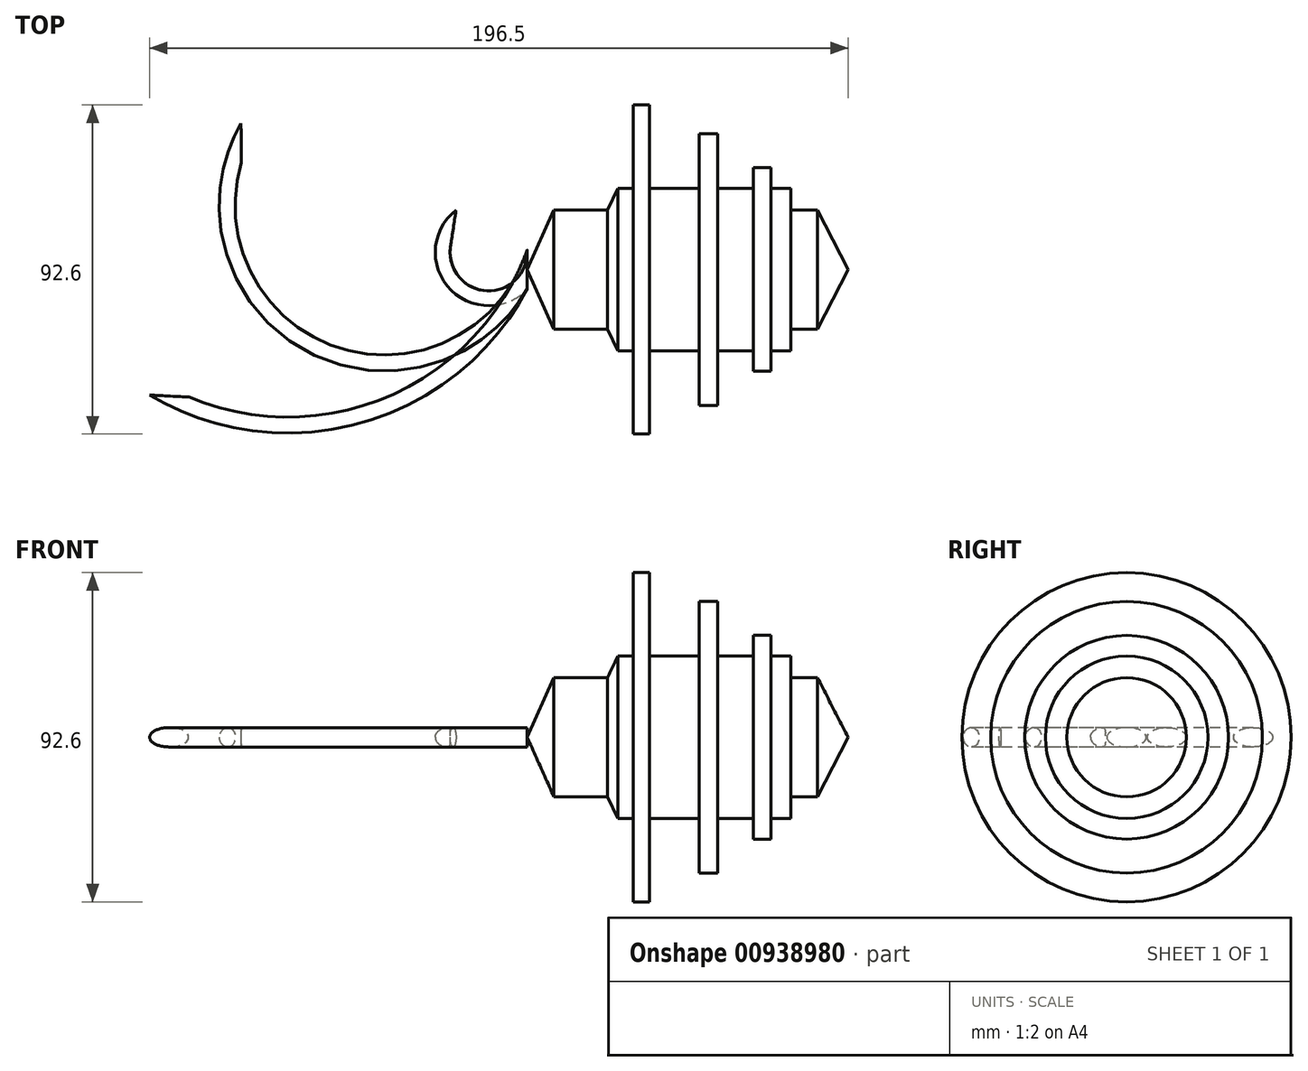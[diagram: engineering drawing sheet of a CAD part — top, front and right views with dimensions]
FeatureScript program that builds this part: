
annotation { "Feature Type Name" : "Feature", "Feature Type Description" : "" }
export const myFeature = defineFeature(function(context is Context, id is Id, definition is map)
    precondition{}
    {
        {
            var Q0;
            Q0=qCreatedBy(makeId("Top.planeOp"),FACE);
            var sketch = newSketch(context, id + "F0", { "sketchPlane" : qUnion([Q0])});
            skLineSegment(sketch, "E0", {"start": v(0, 0) * mm, "end": v(7.52, 16.78) * mm});
            skLineSegment(sketch, "E1", {"start": v(7.52, 16.78) * mm, "end": v(22.57, 16.78) * mm});
            skLineSegment(sketch, "E2", {"start": v(22.57, 16.78) * mm, "end": v(25.46, 22.86) * mm});
            skLineSegment(sketch, "E3", {"start": v(25.46, 22.86) * mm, "end": v(29.8, 22.86) * mm});
            skLineSegment(sketch, "E4", {"start": v(29.8, 22.86) * mm, "end": v(29.8, 46.3) * mm});
            skLineSegment(sketch, "E5", {"start": v(29.8, 46.3) * mm, "end": v(34.43, 46.3) * mm});
            skLineSegment(sketch, "E6", {"start": v(34.43, 46.3) * mm, "end": v(34.43, 22.86) * mm});
            skLineSegment(sketch, "E7", {"start": v(34.43, 22.86) * mm, "end": v(48.32, 22.86) * mm});
            skLineSegment(sketch, "E8", {"start": v(48.32, 22.86) * mm, "end": v(48.32, 38.2) * mm});
            skLineSegment(sketch, "E9", {"start": v(48.32, 38.2) * mm, "end": v(53.53, 38.2) * mm});
            skLineSegment(sketch, "E10", {"start": v(53.53, 38.2) * mm, "end": v(53.53, 22.86) * mm});
            skLineSegment(sketch, "E11", {"start": v(53.53, 22.86) * mm, "end": v(63.66, 22.86) * mm});
            skLineSegment(sketch, "E12", {"start": v(63.66, 22.86) * mm, "end": v(63.66, 28.65) * mm});
            skLineSegment(sketch, "E13", {"start": v(63.66, 28.65) * mm, "end": v(68.58, 28.65) * mm});
            skLineSegment(sketch, "E14", {"start": v(68.58, 28.65) * mm, "end": v(68.58, 22.86) * mm});
            skLineSegment(sketch, "E15", {"start": v(68.58, 22.86) * mm, "end": v(74.08, 22.86) * mm});
            skLineSegment(sketch, "E16", {"start": v(74.08, 22.86) * mm, "end": v(74.08, 16.78) * mm});
            skLineSegment(sketch, "E17", {"start": v(74.08, 16.78) * mm, "end": v(81.6, 16.78) * mm});
            skLineSegment(sketch, "E18", {"start": v(81.6, 16.78) * mm, "end": v(90.28, 0) * mm});
            skArc(sketch, "E19", {"start": v(0, 0) * mm, "mid": v(-44.19, -7.67) * mm, "end": v(-34.72, 36.17) * mm});
            skArc(sketch, "E20", {"start": v(0, 0) * mm, "mid": v(-57.93, -22.23) * mm, "end": v(-80.44, 35.6) * mm});
            skArc(sketch, "E21", {"start": v(0, 0) * mm, "mid": v(-42.72, -39.37) * mm, "end": v(-100.7, -35.6) * mm});
            skArc(sketch, "E22", {"start": v(0, 0) * mm, "mid": v(-16.5, -5.59) * mm, "end": v(-20.83, 11.29) * mm});
            skLineSegment(sketch, "E23", {"start": v(0, 0) * mm, "end": v(90.28, 0) * mm});
            skSolve(sketch);
        }
        {
            var Q0;
            Q0=qCreatedBy(makeId("Right.planeOp"),FACE);
            var sketch = newSketch(context, id + "F1", { "sketchPlane" : qUnion([Q0])});
            skEllipse(sketch, "E24", {"center": v(0, 0) * mm, "majorRadius": 5.53 * mm, "minorRadius": 2.73 * mm, "majorAxis": v(-1, 0)});
            skSolve(sketch);
        }
        {
            var Q0;
            Q0=makeQuery(id+"F0.imprint","IMPRINT",FACE,{"disambiguationData":[TD([[makeQuery(id+"F0.imprint","IMPRINT",EDGE,{"derivedFrom":sQuery(id+"F0.wireOp",EDGE,"E0")}),-1.0]])]});
            var Q1;
            Q1=sQuery(id+"F0.wireOp",EDGE,"E23");
            revolve(context, id + "F2", {"surfaceOperationType" : NewSurfaceOperationType.NEW, "entities" : qUnion([Q0]), "axis" : qUnion([Q1]), "revolveType" : RevolveType.FULL});
        }
        {
            var Q0;
            Q0=makeQuery(id+"F1.imprint","IMPRINT",FACE,{"disambiguationData":[TD([[makeQuery(id+"F1.imprint","IMPRINT",EDGE,{"derivedFrom":sQuery(id+"F1.wireOp",EDGE,"E24")}),1.0]])]});
            var Q1;
            Q1=sQuery(id+"F0.wireOp",EDGE,"E22");
            sweep(context, id + "F3", {"profiles" : qUnion([Q0]), "path" : qUnion([Q1])});
        }
        {
            var Q0;
            Q0=makeQuery(id+"F3.opSweep","CAP_FACE",FACE,{"disambiguationData":[OSD([sQuery(id+"F0.wireOp",VERTEX,"E22.start"),sQuery(id+"F1.wireOp",EDGE,"E24")])],"isStart":true});
            var Q1;
            Q1=sQuery(id+"F0.wireOp",EDGE,"E20");
            sweep(context, id + "F4", {"profiles" : qUnion([Q0]), "path" : qUnion([Q1])});
        }
        {
            var Q0;
            Q0=makeQuery(id+"F3.opSweep","CAP_FACE",FACE,{"disambiguationData":[OSD([sQuery(id+"F0.wireOp",VERTEX,"E22.start"),sQuery(id+"F1.wireOp",EDGE,"E24")])],"isStart":true});
            var Q1;
            Q1=sQuery(id+"F0.wireOp",EDGE,"E21");
            sweep(context, id + "F5", {"profiles" : qUnion([Q0]), "path" : qUnion([Q1])});
        }
    });
